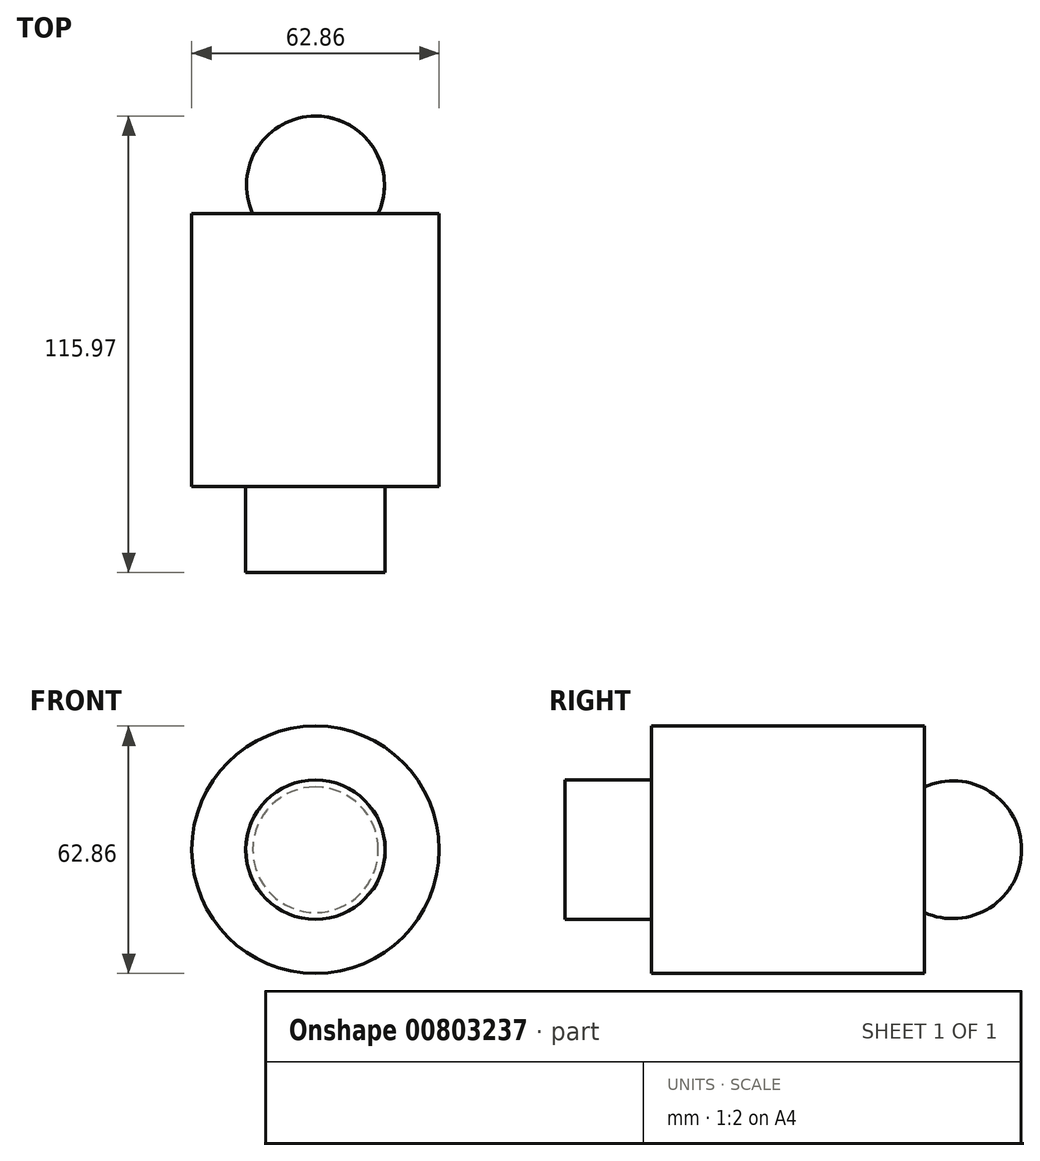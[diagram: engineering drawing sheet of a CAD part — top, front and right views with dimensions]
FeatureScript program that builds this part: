
annotation { "Feature Type Name" : "Feature", "Feature Type Description" : "" }
export const myFeature = defineFeature(function(context is Context, id is Id, definition is map)
    precondition{}
    {
        {
            var Q0;
            Q0=qCreatedBy(makeId("Top.planeOp"),FACE);
            var sketch = newSketch(context, id + "F0", { "sketchPlane" : qUnion([Q0])});
            skLineSegment(sketch, "E0", {"start": v(0, 76.2) * mm, "end": v(0, 0) * mm, "construction": true});
            skLineSegment(sketch, "E1", {"start": v(0, 0) * mm, "end": v(0, -75.1) * mm, "construction": true});
            skLineSegment(sketch, "E2.bottom", {"start": v(15.95, 49.5) * mm, "end": v(31.43, 49.5) * mm});
            skLineSegment(sketch, "E2.top", {"start": v(17.7, -19.84) * mm, "end": v(31.43, -19.84) * mm});
            skLineSegment(sketch, "E2.left", {"start": v(0, 49.5) * mm, "end": v(0, -19.84) * mm});
            skLineSegment(sketch, "E2.right", {"start": v(31.43, 49.5) * mm, "end": v(31.43, -19.84) * mm});
            skLineSegment(sketch, "E3.top", {"start": v(0, -41.72) * mm, "end": v(17.7, -41.72) * mm});
            skLineSegment(sketch, "E3.left", {"start": v(0, -10.94) * mm, "end": v(0, -41.72) * mm});
            skLineSegment(sketch, "E3.right", {"start": v(17.7, -19.84) * mm, "end": v(17.7, -41.72) * mm});
            skArc(sketch, "E4", {"start": v(15.95, 49.5) * mm, "mid": v(14.72, 66.23) * mm, "end": v(0, 74.25) * mm});
            skLineSegment(sketch, "E5", {"start": v(0, 74.25) * mm, "end": v(0, -41.72) * mm});
            skSolve(sketch);
        }
        {
            var Q0;
            Q0=makeQuery(id+"F0.imprint","IMPRINT",FACE,{"disambiguationData":[TD([[makeQuery(id+"F0.imprint","IMPRINT",EDGE,{"derivedFrom":sQuery(id+"F0.wireOp",EDGE,"E2.bottom")}),-1.0]])]});
            var Q1;
            Q1=sQuery(id+"F0.wireOp",EDGE,"E5");
            revolve(context, id + "F1", {"surfaceOperationType" : NewSurfaceOperationType.NEW, "entities" : qUnion([Q0]), "axis" : qUnion([Q1]), "revolveType" : RevolveType.FULL});
        }
    });
